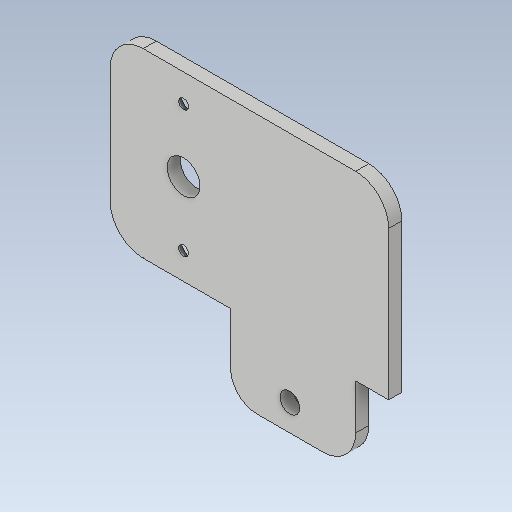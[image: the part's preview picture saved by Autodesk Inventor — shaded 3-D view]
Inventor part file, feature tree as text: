
AUTODESK INVENTOR PART (.ipt)
format: ipt  version: 2020 (Build 240168000, 168)  size: 121,856 bytes
history: native  units: mm
features: chamfer x2, other x1, extrude x1, sketch x1
ambient origin geometry x8: Origin, YZ Plane, XZ Plane, XY Plane, X Axis, Y Axis, Z Axis, Center Point
bodies: Body1 (feature_tree)
feature tree (5):
  other  "Твердое тело1"
  extrude  "Выдавливание1"  Depth=5.0mm
  chamfer  "Фаска3"  Distance=2.0mm
  chamfer  "Фаска4"  Distance=2.0mm Angle=45.0deg
  sketch  "Эскиз1"
